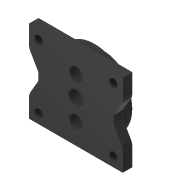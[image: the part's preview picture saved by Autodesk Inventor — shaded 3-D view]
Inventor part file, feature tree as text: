
AUTODESK INVENTOR PART (.ipt)
format: ipt  version: 2017 (Build 210142000, 142)  size: 219,648 bytes
history: native  units: in
note: dims shown in document units (in); Inventor stores cm internally (conversion verified against a paired STEP export)
features: extrude x12, sketch x11, other x4, plane x2, reference x2, projected_geometry x2, mirror x1
ambient origin geometry x8: Origin, YZ Plane, XZ Plane, XY Plane, X Axis, Y Axis, Z Axis, Center Point
bodies: Solid1 (feature_tree)
feature tree (34):
  plane  "Work Plane1"
  extrude  "Extrusion1"  Depth=0.125in
  extrude  "Extrusion2"  Depth=0.125in
  extrude  "Extrusion3"  Depth=0.125in
  sketch  "Sketch4"  dims[d9=1.0in d10=0.0in d11=0.125in d12=0.0in]
  plane  "Work Plane2"
  extrude  "Extrusion4"  Depth=0.125in TaperAngle=0.0deg
  extrude  "Extrusion5"  Depth=0.125in
  extrude  "Extrusion6"  Depth=0.25in
  extrude  "Extrusion8"  Depth=0.125in
  extrude  "Extrusion9"  Depth=0.125in TaperAngle=0.0deg
  sketch  "Sketch10"  dims[d29=0.125in d30=0.125in]
  extrude  "Extrusion10"  Depth=0.125in
  extrude  "Extrusion11"  Depth=0.125in
  extrude  "Extrusion12"  Depth=0.125in TaperAngle=0.0deg
  mirror  "Mirror1"
  extrude  "Extrusion13"  Depth=1.0in
  sketch  "Sketch1"  dims[d0=0.125in d1=0.0in d2=0.7106in]
  reference  "Reference1"
  sketch  "Sketch2"  dims[d3=0.125in d4=0.0in d5=0.2in]
  sketch  "Sketch3"  dims[d6=0.125in d7=0.0in d8=0.125in]
  sketch  "Sketch5"  dims[d13=0.125in d14=0.0in d21=0.125in]
  projected_geometry  "Projected Loop1"
  sketch  "Sketch6"  dims[d22=0.125in d23=0.25in]
  sketch  "Sketch8"  dims[d24=0.125in d25=0.125in]
  reference  "Reference2"
  projected_geometry  "Projected Loop2"
  sketch  "Sketch9"  dims[d26=0.25in d27=0.125in d28=0.0in]
  sketch  "Sketch11"  dims[d31=0.11in d32=0.125in]
  sketch  "Sketch12"  dims[d33=0.125in d34=0.125in d35=0.0in d36=0.2in d37=0.18in d38=0.18in d39=0.275in d40=0.275in d41=0.125in d42=0.0in d43=0.2188in d44=0.0in d45=0.1in d46=0.1875in d47=0.0in d48=1.0in d49=0.0in]
  parser-record x1  (decoder bookkeeping rows leaked as tree rows — omitted from the tree; the rows remain in map.json)
  other  "Assembly1.iam"
  other  "Cap:1"
  other  "Case:1"
note: 1 file-system path scrubbed to <path> (originals preserved in map.json)
